# Revit family: RN 80110 Optipress-Rubinetto a sfera
name_source: partatom
category: Rohrzubehör
units: mm (PartAtom-declared; Revit-internal decimal feet)

## family parameters
Arbeitsebenenbasiert = Nein
Beim Laden mit Abzugskörper schneiden = Nein
Bemaßung runder Anschluss = Durchmesser verwenden
Gemeinsam genutzt = Nein
Immer vertikal = Ja
Teiletyp = Ventil - Zerlegung in

## types (7) — shared parameters
1.010.00.2 Number of the part of the guideline = 2
1.010.00.3 Issue date (month) of the guideline = 201601
1.010.00.4 Manufacturer name = R. Nussbaum AG
1.010.00.5 Revision date of the file = 20190514
1.100.00.3 Sort number for display sequence = 4
1.100.00.4 Product designation = Rubinetti di chiusura e di regolazione
1.960/3L.00.8 Link (URL) = https://www.nussbaum.ch
2.700.00.4 valve assembly type = 11
2.700.00.7 maximum operating temperature TB [°C] = 90
2.700.00.8 maximum operating pressure(working pressure) ps [1.0 · 102 Pa] = 16
Connector Visibility = Nein
EnclosingSpace Visibility = Nein

## per-type parameters (varying)
| type | 1.800.00.3 BS number | 1.810.00.3 Manufacturer’s reference number | 1.810.00.4 DATANORM number | 1.810.00.6 GTIN number | 2.700.00.26 product description | 2.700.00.5 nominal size DN | 2.700.00.6 kvs-value [m3/h] | CONNECTOR0_DIAMETER_dX_0r | CONNECTOR0_dX_00 | CONNECTOR0_dX_01 | CONNECTOR0_ref_dX | CONNECTOR1_DIAMETER_dX_0r | CONNECTOR1_dX_00 | CONNECTOR1_dX_01 | CONNECTOR1_ref_dX | R. Nussbaum AG 80110.22 it Visibility | R. Nussbaum AG 80110.23 it Visibility | R. Nussbaum AG 80110.24 it Visibility | R. Nussbaum AG 80110.25 it Visibility | R. Nussbaum AG 80110.26 it Visibility | R. Nussbaum AG 80110.27 it Visibility | R. Nussbaum AG 80110.28 it Visibility |
| DN 10 | 0040270000000000000000000000090070000000000000000100000000 | 80110.22 | 80110.22 | 7612945710734 | 80110.22, Optipress-Rubinetto a sfera, corpo a 3 componenti, DN=10 | 10 | 10 | 10 mm  [stored 0.0328084 ft] | 68 mm | 46 mm | 46 mm | 10 mm  [stored 0.0328084 ft] | 46 mm | 68 mm | 46 mm | Ja | Nein | Nein | Nein | Nein | Nein | Nein |
| DN 15 | 0040270000000000000000000000090070000000000000000200000000 | 80110.23 | 80110.23 | 7612945710741 | 80110.23, Optipress-Rubinetto a sfera, corpo a 3 componenti, DN=15 | 15 | 33 | 15 mm | 68 mm | 46 mm | 46 mm | 15 mm | 46 mm | 68 mm | 46 mm | Nein | Ja | Nein | Nein | Nein | Nein | Nein |
| DN 20 | 0040270000000000000000000000090070000000000000000300000000 | 80110.24 | 80110.24 | 7612945710758 | 80110.24, Optipress-Rubinetto a sfera, corpo a 3 componenti, DN=20 | 20 | 47 | 20 mm | 74 mm | 50 mm  [stored 0.164042 ft] | 50 mm  [stored 0.164042 ft] | 20 mm | 50 mm  [stored 0.164042 ft] | 74 mm | 50 mm  [stored 0.164042 ft] | Nein | Nein | Ja | Nein | Nein | Nein | Nein |
| DN 25 | 0040270000000000000000000000090070000000000000000400000000 | 80110.25 | 80110.25 | 7612945710765 | 80110.25, Optipress-Rubinetto a sfera, corpo a 3 componenti, DN=25 | 25 | 54 | 25 mm  [stored 0.082021 ft] | 78 mm | 54 mm | 54 mm | 25 mm  [stored 0.082021 ft] | 54 mm | 78 mm | 54 mm | Nein | Nein | Nein | Ja | Nein | Nein | Nein |
| DN 32 | 0040270000000000000000000000090070000000000000000500000000 | 80110.26 | 80110.26 | 7612945710772 | 80110.26, Optipress-Rubinetto a sfera, corpo a 3 componenti, DN=32 | 32 | 82 | 32 mm  [stored 0.104987 ft] | 84 mm | 58 mm  [stored 0.190289 ft] | 58 mm  [stored 0.190289 ft] | 32 mm  [stored 0.104987 ft] | 58 mm  [stored 0.190289 ft] | 84 mm | 58 mm  [stored 0.190289 ft] | Nein | Nein | Nein | Nein | Ja | Nein | Nein |
| DN 40 | 0040270000000000000000000000090070000000000000000600000000 | 80110.27 | 80110.27 | 7612945710789 | 80110.27, Optipress-Rubinetto a sfera, corpo a 3 componenti, DN=40 | 40 | 160 | 40 mm | 113 mm | 77 mm | 77 mm | 40 mm | 77 mm | 113 mm | 77 mm | Nein | Nein | Nein | Nein | Nein | Ja | Nein |
| DN 50 | 0040270000000000000000000000090070000000000000000700000000 | 80110.28 | 80110.28 | 7612945710796 | 80110.28, Optipress-Rubinetto a sfera, corpo a 3 componenti, DN=50 | 50 | 230 | 50 mm  [stored 0.164042 ft] | 123 mm | 88 mm | 88 mm | 50 mm  [stored 0.164042 ft] | 88 mm | 123 mm | 88 mm | Nein | Nein | Nein | Nein | Nein | Nein | Ja |

note: [stored X ft] marks values corroborated as IEEE doubles in the binary element streams (Revit-internal decimal feet)

## geometry (parser evidence)
native form markers: Sweep x2
no freeform markers — native parametric forms only
